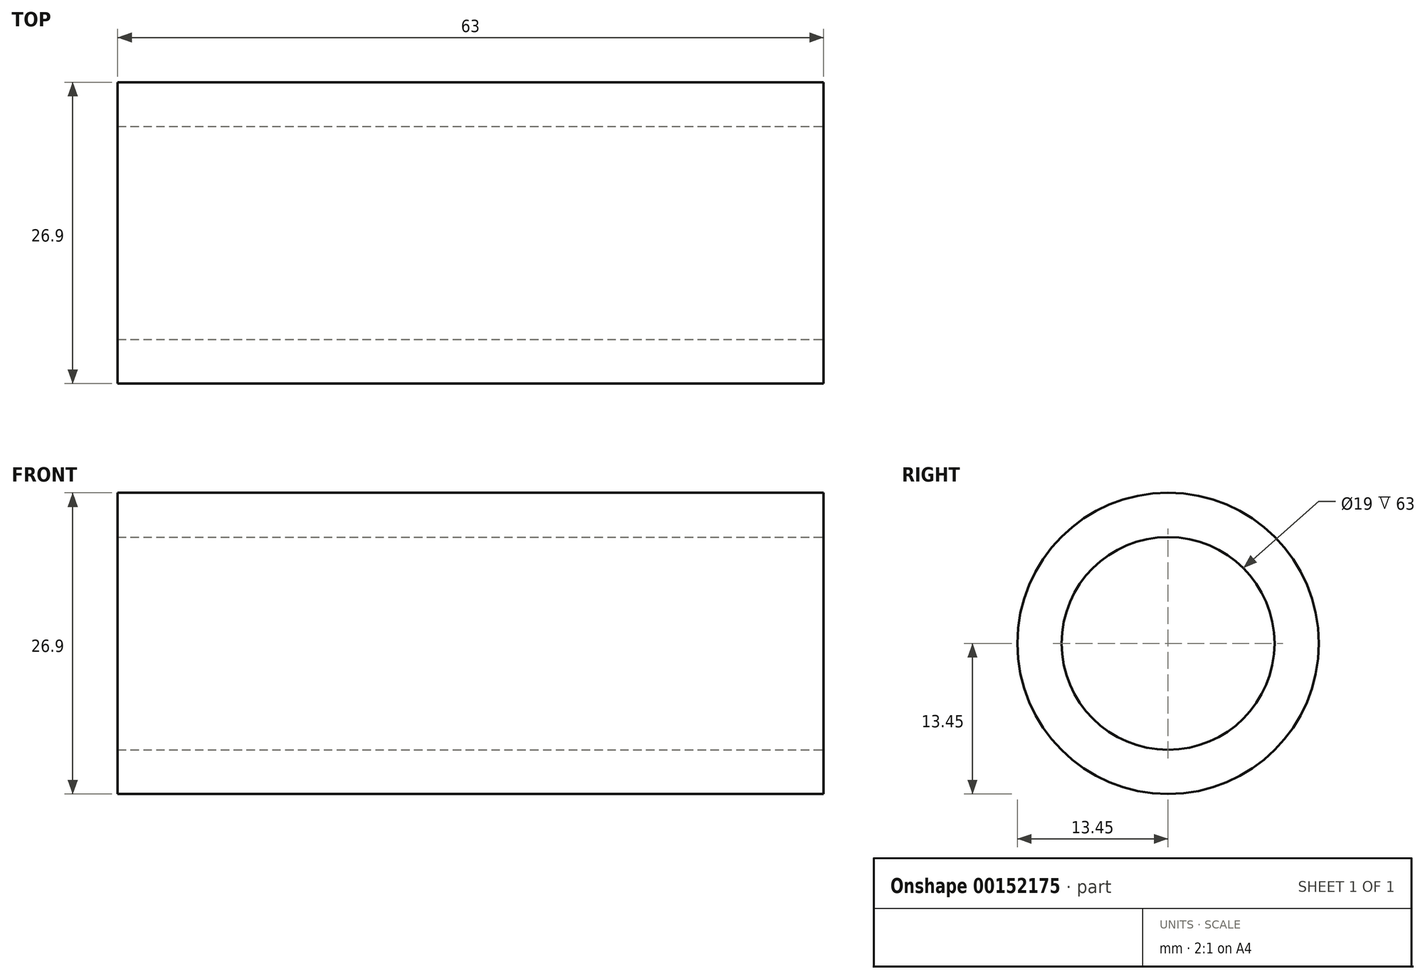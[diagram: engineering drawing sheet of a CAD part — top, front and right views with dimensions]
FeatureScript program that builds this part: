
annotation { "Feature Type Name" : "Feature", "Feature Type Description" : "" }
export const myFeature = defineFeature(function(context is Context, id is Id, definition is map)
    precondition{}
    {
        {
            var Q0;
            Q0=qCreatedBy(makeId("Right.planeOp"),FACE);
            var sketch = newSketch(context, id + "F0", { "sketchPlane" : qUnion([Q0])});
            skCircle(sketch, "E0", {"center": v(0, 0) * mm, "radius": 13.45 * mm});
            skCircle(sketch, "E1", {"center": v(0, 0) * mm, "radius": 9.5 * mm});
            skSolve(sketch);
        }
        {
            var Q0;
            Q0=qSketchRegion(id+"F0",true);
            extrude(context, id + "F1", {"entities" : qUnion([Q0]), "oppositeDirection" : true, "depth" : 63 * mm});
        }
    });
